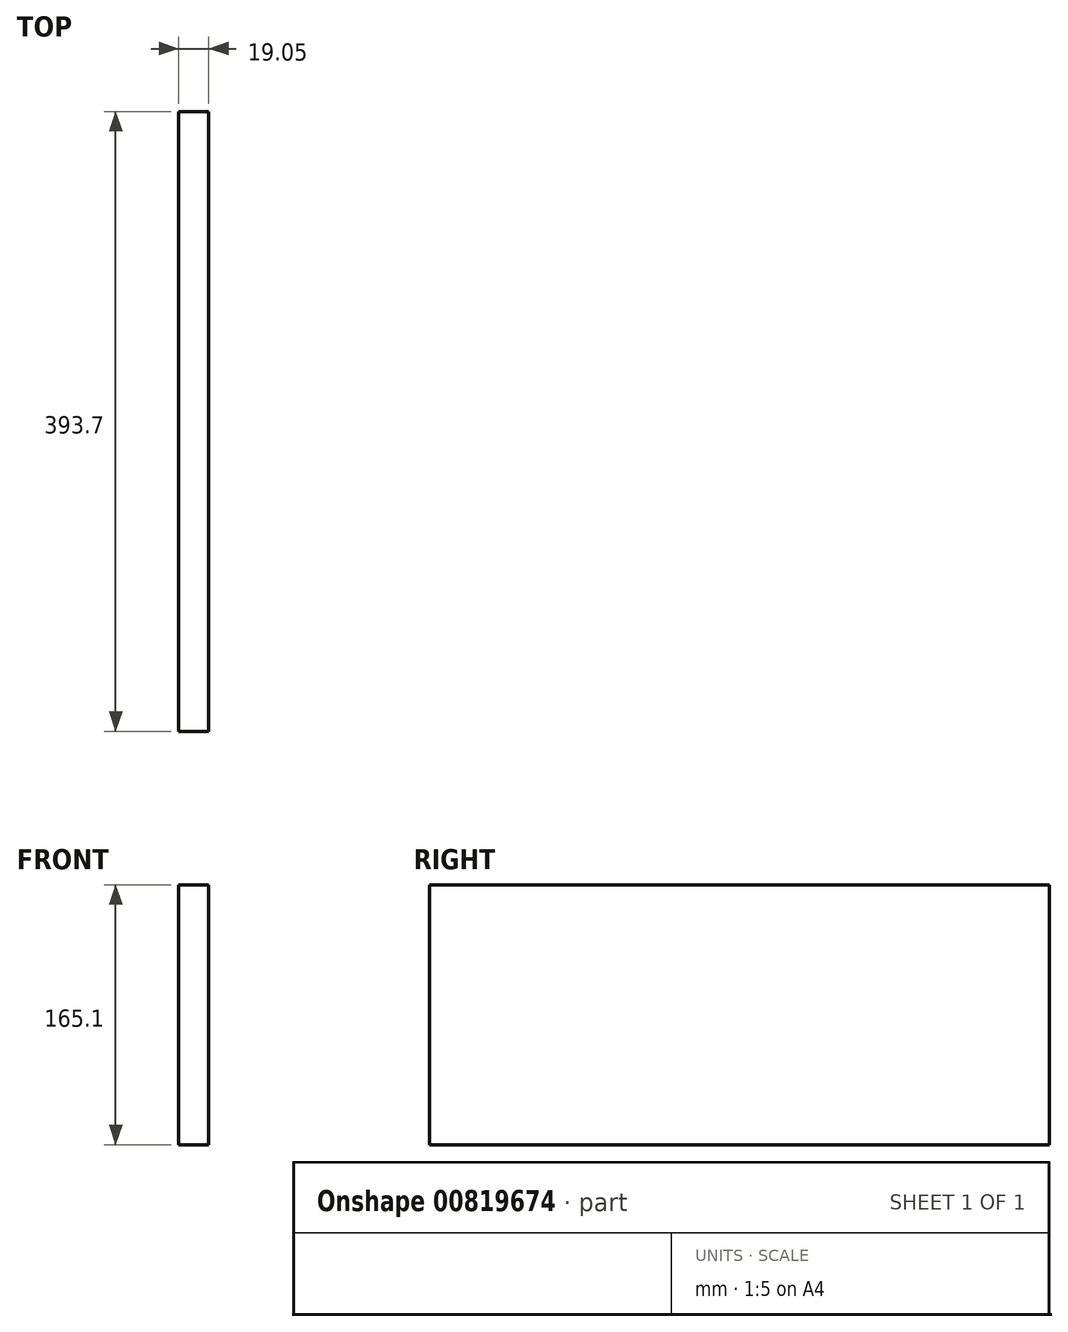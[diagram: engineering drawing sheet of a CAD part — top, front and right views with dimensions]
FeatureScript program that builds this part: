
annotation { "Feature Type Name" : "Feature", "Feature Type Description" : "" }
export const myFeature = defineFeature(function(context is Context, id is Id, definition is map)
    precondition{}
    {
        {
            var Q0;
            Q0=qCreatedBy(makeId("Front.planeOp"),FACE);
            var sketch = newSketch(context, id + "F0", { "sketchPlane" : qUnion([Q0])});
            skLineSegment(sketch, "E0.bottom", {"start": v(0, 0) * mm, "end": v(-19.05, 0) * mm});
            skLineSegment(sketch, "E0.top", {"start": v(0, 165.1) * mm, "end": v(-19.05, 165.1) * mm});
            skLineSegment(sketch, "E0.left", {"start": v(0, 0) * mm, "end": v(0, 165.1) * mm});
            skLineSegment(sketch, "E0.right", {"start": v(-19.05, 0) * mm, "end": v(-19.05, 165.1) * mm});
            skSolve(sketch);
        }
        {
            var Q0;
            Q0=makeQuery(id+"F0.imprint","IMPRINT",FACE,{"disambiguationData":[TD([[makeQuery(id+"F0.imprint","IMPRINT",EDGE,{"derivedFrom":sQuery(id+"F0.wireOp",EDGE,"E0.bottom")}),-1.0]])]});
            extrude(context, id + "F1", {"entities" : qUnion([Q0]), "depth" : 393.7 * mm, "offsetDistance" : 25.4 * mm});
        }
    });
